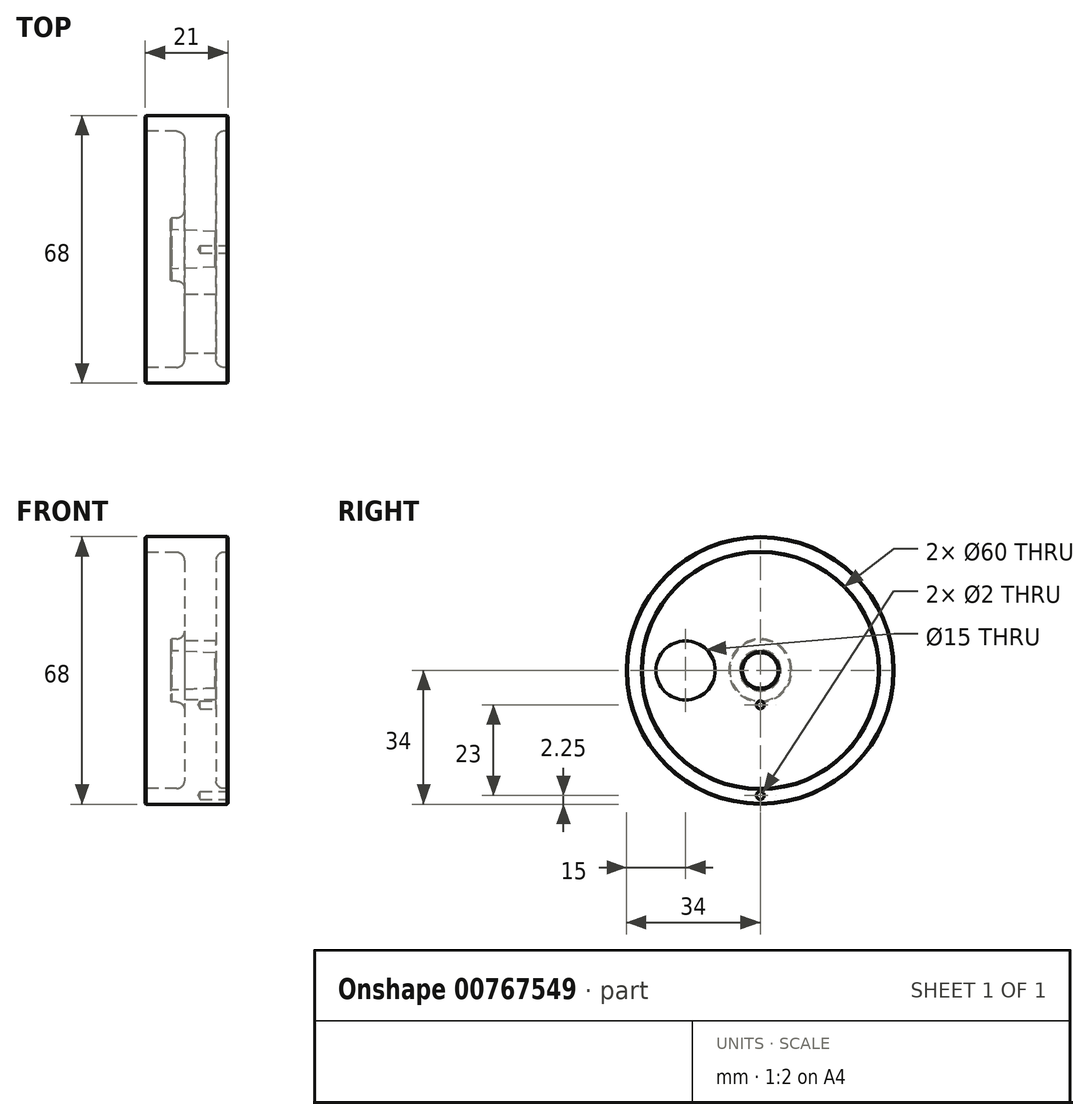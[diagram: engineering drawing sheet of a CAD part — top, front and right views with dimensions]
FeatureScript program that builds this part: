
annotation { "Feature Type Name" : "Feature", "Feature Type Description" : "" }
export const myFeature = defineFeature(function(context is Context, id is Id, definition is map)
    precondition{}
    {
        {
            var Q0;
            Q0=qCreatedBy(makeId("Front.planeOp"),FACE);
            var sketch = newSketch(context, id + "F0", { "sketchPlane" : qUnion([Q0])});
            skLineSegment(sketch, "E0", {"start": v(0, 5) * mm, "end": v(0, 8) * mm});
            skLineSegment(sketch, "E1", {"start": v(0, 8) * mm, "end": v(1.5, 8) * mm});
            skLineSegment(sketch, "E2", {"start": v(3.5, 10) * mm, "end": v(3.5, 28) * mm});
            skLineSegment(sketch, "E3", {"start": v(1.5, 30) * mm, "end": v(-6.5, 30) * mm});
            skLineSegment(sketch, "E4", {"start": v(-6.5, 30) * mm, "end": v(-6.5, 34) * mm});
            skLineSegment(sketch, "E5", {"start": v(-6.5, 34) * mm, "end": v(14.5, 34) * mm});
            skLineSegment(sketch, "E6", {"start": v(14.5, 34) * mm, "end": v(14.5, 30) * mm});
            skLineSegment(sketch, "E7", {"start": v(14.5, 30) * mm, "end": v(13.5, 30) * mm});
            skLineSegment(sketch, "E8", {"start": v(11.5, 28) * mm, "end": v(11.5, 4.5) * mm});
            skLineSegment(sketch, "E9", {"start": v(11.5, 4.5) * mm, "end": v(0, 5) * mm});
            skLineSegment(sketch, "E10", {"start": v(0, 0) * mm, "end": v(11.5, 0) * mm, "construction": true});
            skPoint(sketch, "E11.visualSharp", {"position": v(3.5, 30) * mm});
            skArc(sketch, "E11.filletArc", {"start": v(3.5, 28) * mm, "mid": v(2.91, 29.41) * mm, "end": v(1.5, 30) * mm});
            skPoint(sketch, "E12.visualSharp", {"position": v(11.5, 30) * mm});
            skArc(sketch, "E12.filletArc", {"start": v(13.5, 30) * mm, "mid": v(12.09, 29.41) * mm, "end": v(11.5, 28) * mm});
            skPoint(sketch, "E13.visualSharp", {"position": v(3.5, 8) * mm});
            skArc(sketch, "E13.filletArc", {"start": v(1.5, 8) * mm, "mid": v(2.91, 8.59) * mm, "end": v(3.5, 10) * mm});
            skSolve(sketch);
        }
        {
            var Q0;
            Q0 = qSketchRegion(id + "F0", true);
            var Q1;
            Q1=sQuery(id+"F0.wireOp",EDGE,"E10");
            revolve(context, id + "F1", {"surfaceOperationType" : NewSurfaceOperationType.NEW, "entities" : qUnion([Q0]), "axis" : qUnion([Q1]), "revolveType" : RevolveType.FULL});
        }
        {
            var Q0;
            Q0=makeQuery(id+"F1.opRevolve","SWEPT_FACE",FACE,{"disambiguationData":[OSD([sQuery(id+"F0.wireOp",EDGE,"E4")])]});
            var Q1;
            Q1=makeQuery(id+"F1.opRevolve","SWEPT_FACE",FACE,{"disambiguationData":[OSD([sQuery(id+"F0.wireOp",EDGE,"E6")])]});
            var Q2;
            Q2=makeQuery(id+"F1.opRevolve","SWEPT_FACE",FACE,{"disambiguationData":[OSD([sQuery(id+"F0.wireOp",EDGE,"E0")])]});
            var Q3;
            Q3=makeQuery(id+"F1.opRevolve","SWEPT_EDGE",EDGE,{"disambiguationData":[OSD([sQuery(id+"F0.wireOp",EDGE,"E8"),sQuery(id+"F0.wireOp",EDGE,"E9")])]});
            chamfer(context, id + "F2", {"entities" : qUnion([Q0, Q1, Q2, Q3]), "width" : 0.25 * mm, "tangentPropagation" : true});
        }
        {
            var Q0;
            Q0=qCreatedBy(makeId("Right.planeOp"),FACE);
            var sketch = newSketch(context, id + "F3", { "sketchPlane" : qUnion([Q0])});
            skCircle(sketch, "E14", {"center": v(-19, 0) * mm, "radius": 7.5 * mm});
            skSolve(sketch);
        }
        {
            var Q0;
            Q0 = qSketchRegion(id + "F3", true);
            extrude(context, id + "F4", {"entities" : qUnion([Q0]), "operationType" : NewBodyOperationType.REMOVE, "endBound" : BoundingType.SYMMETRIC, "depth" : 25 * mm, "offsetDistance" : 25 * mm});
        }
        {
            var Q0;
            Q0=makeQuery(id+"F1.opRevolve","SWEPT_FACE",FACE,{"disambiguationData":[OSD([sQuery(id+"F0.wireOp",EDGE,"E6")])]});
            var sketch = newSketch(context, id + "F5", { "sketchPlane" : qUnion([Q0])});
            skPoint(sketch, "E15", {"position": v(0, -8.75) * mm});
            skPoint(sketch, "E16", {"position": v(0, -31.75) * mm});
            skSolve(sketch);
        }
        {
            var Q0;
            Q0=sQuery(id+"F5.wireOp",VERTEX,"E16");
            var Q1;
            Q1=sQuery(id+"F5.wireOp",VERTEX,"E15");
            var Q2;
            Q2=makeQuery(id+"F1.opRevolve","SWEPT_BODY",BODY,{"disambiguationData":[OSD([sQuery(id+"F0.wireOp",EDGE,"E0"),sQuery(id+"F0.wireOp",EDGE,"E1"),sQuery(id+"F0.wireOp",EDGE,"E2"),sQuery(id+"F0.wireOp",EDGE,"E3"),sQuery(id+"F0.wireOp",EDGE,"E4"),sQuery(id+"F0.wireOp",EDGE,"E5"),sQuery(id+"F0.wireOp",EDGE,"E6"),sQuery(id+"F0.wireOp",EDGE,"E7"),sQuery(id+"F0.wireOp",EDGE,"E8"),sQuery(id+"F0.wireOp",EDGE,"E9"),sQuery(id+"F0.wireOp",EDGE,"E11.filletArc"),sQuery(id+"F0.wireOp",EDGE,"E12.filletArc"),sQuery(id+"F0.wireOp",EDGE,"E13.filletArc")])]});
            hole(context, id + "F6", {"style" : HoleStyle.SIMPLE, "endStyle" : HoleEndStyle.BLIND, "holeDiameter" : 2 * mm, "majorDiameter" : 5 * mm, "holeDepth" : 7 * mm, "tappedDepth" : 6 * mm, "tapClearance" : 0, "startFromSketch" : true, "locations" : qUnion([Q0, Q1]), "scope" : qUnion([Q2])});
        }
    });
